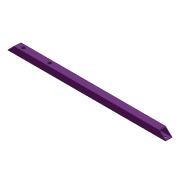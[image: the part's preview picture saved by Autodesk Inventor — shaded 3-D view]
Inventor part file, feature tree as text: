
AUTODESK INVENTOR PART (.ipt)
format: ipt  version: 2012 (Build 160160000, 160)  size: 119,808 bytes
history: native  units: in
note: dims shown in document units (in); Inventor stores cm internally (conversion verified against a paired STEP export)
features: extrude x5, sketch x5, shell x1
ambient origin geometry x8: Origin, YZ Plane, XZ Plane, XY Plane, X Axis, Y Axis, Z Axis, Center Point
bodies: Solid1 (feature_tree)
feature tree (11):
  extrude  "Extrusion1"  Depth=24.0in
  shell  "Shell1"  Thickness=1.0in
  extrude  "Extrusion2"  Depth=1.0in
  extrude  "Extrusion3"  Depth=1.0in
  extrude  "Extrusion5"  Depth=1.0in TaperAngle=0.0deg
  extrude  "Extrusion6"  Depth=0.5in
  sketch  "Sketch1"  dims[d0=1.0in d1=24.0in d2=1.0in d3=0.0in]
  sketch  "Sketch2"  dims[d4=0.0625in d5=1.0in]
  sketch  "Sketch3"  dims[d6=0.0625in d7=1.0in]
  sketch  "Sketch5"  dims[d8=0.0625in d9=1.0in d10=0.0in]
  sketch  "Sketch6"  dims[d11=0.5in d12=0.5in d13=0.25in d14=0.5in d15=0.5in d16=1.0in d17=0.0in d23=0.25in d25=1.875in d26=4.0in d27=1.0in d28=0.0in d29=0.5in d30=0.5in d31=1.0in d32=0.0in]
